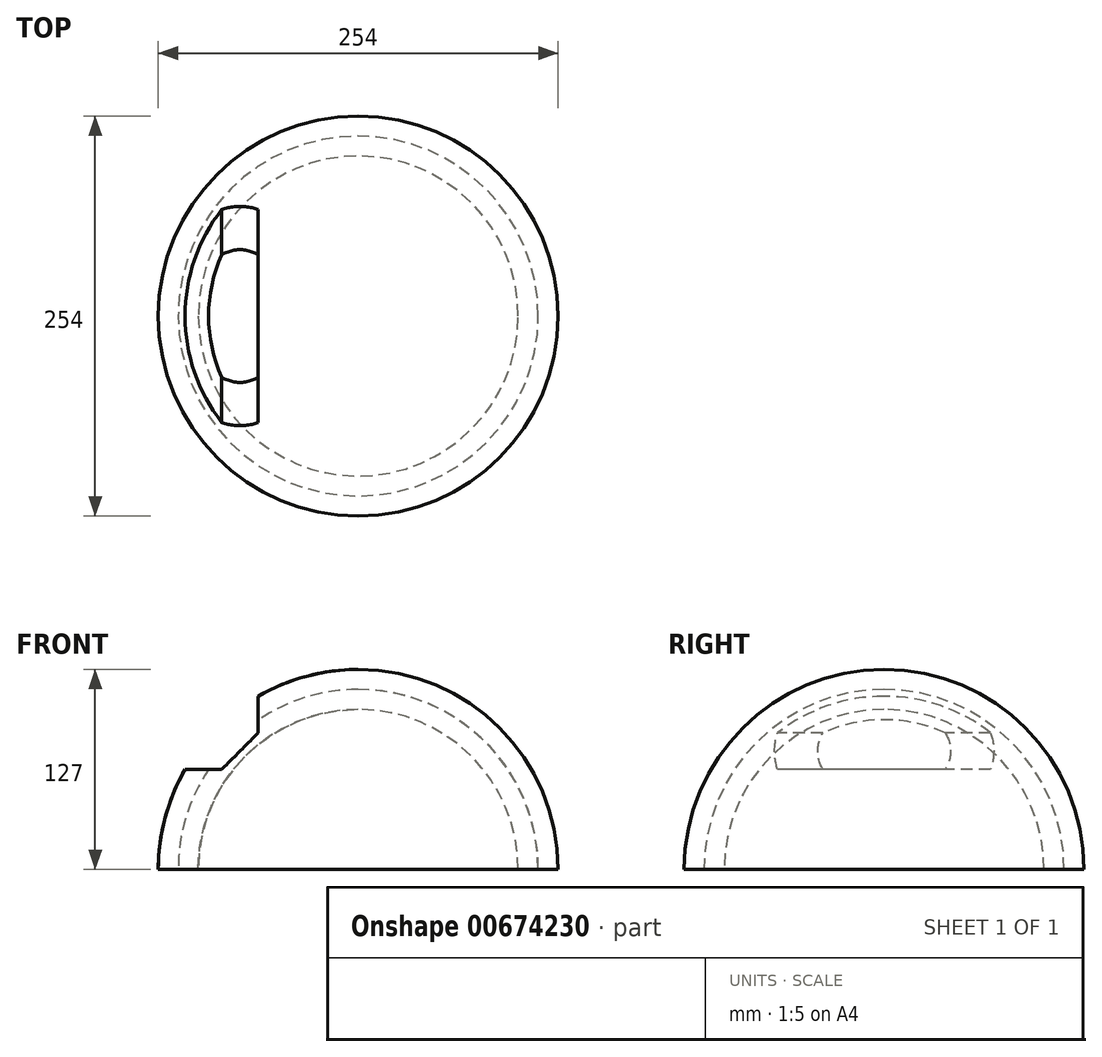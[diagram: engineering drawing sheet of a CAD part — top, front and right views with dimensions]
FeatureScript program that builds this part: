
annotation { "Feature Type Name" : "Feature", "Feature Type Description" : "" }
export const myFeature = defineFeature(function(context is Context, id is Id, definition is map)
    precondition{}
    {
        {
            var Q0;
            Q0=qCreatedBy(makeId("Front.planeOp"),FACE);
            var sketch = newSketch(context, id + "F0", { "sketchPlane" : qUnion([Q0])});
            skLineSegment(sketch, "E0.bottom", {"start": v(63.5, 63.5) * mm, "end": v(63.5, 63.5) * mm});
            skLineSegment(sketch, "E0.top", {"start": v(63.5, -63.5) * mm, "end": v(-63.5, -63.5) * mm});
            skLineSegment(sketch, "E0.left", {"start": v(63.5, 63.5) * mm, "end": v(63.5, -63.5) * mm});
            skLineSegment(sketch, "E0.right", {"start": v(-63.5, -63.5) * mm, "end": v(-63.5, -63.5) * mm});
            skPoint(sketch, "E0.middle", {"position": v(0, 0) * mm});
            skPoint(sketch, "E1.visualSharp", {"position": v(-63.5, 63.5) * mm});
            skArc(sketch, "E1.filletArc", {"start": v(63.5, 63.5) * mm, "mid": v(-26.3, 26.3) * mm, "end": v(-63.5, -63.5) * mm});
            skPoint(sketch, "E2.MirrorCS.end.orphan", {"position": v(-46.49, 0) * mm});
            skArc(sketch, "E3.0", {"start": v(63.5, 50.8) * mm, "mid": v(-17.32, 17.32) * mm, "end": v(-50.8, -63.5) * mm});
            skArc(sketch, "E4.0", {"start": v(63.5, 38.1) * mm, "mid": v(-8.34, 8.34) * mm, "end": v(-38.1, -63.5) * mm});
            skSolve(sketch);
        }
        {
            var Q0;
            {var subQ0=sQuery(id+"F0.wireOp",EDGE,"E1.filletArc");Q0=makeQuery(id+"F0.imprint","IMPRINT",FACE,{"disambiguationData":[TD([[makeQuery(id+"F0.imprint","IMPRINT",EDGE,{"derivedFrom":subQ0}),1.0]])]});}
            var Q1;
            {var subQ3=sQuery(id+"F0.wireOp",EDGE,"E4.0");Q1=makeQuery(id+"F0.imprint","IMPRINT",FACE,{"disambiguationData":[TD([[makeQuery(id+"F0.imprint","IMPRINT",EDGE,{"derivedFrom":subQ3}),1.0]])]});}
            var Q2;
            Q2=sQuery(id+"F0.wireOp",EDGE,"E0.left");
            revolve(context, id + "F1", {"entities" : qUnion([Q0, Q1]), "axis" : qUnion([Q2]), "revolveType" : RevolveType.FULL});
        }
        {
            var Q0;
            Q0=qCreatedBy(makeId("Front.planeOp"),FACE);
            var sketch = newSketch(context, id + "F2", { "sketchPlane" : qUnion([Q0])});
            skArc(sketch, "E5", {"start": v(190.5, -63.5) * mm, "mid": v(63.5, 63.5) * mm, "end": v(-63.5, -63.5) * mm});
            skLineSegment(sketch, "E6", {"start": v(-46.49, 0) * mm, "end": v(0, 46.49) * mm});
            skLineSegment(sketch, "E7", {"start": v(0, 46.49) * mm, "end": v(0, 23.24) * mm});
            skLineSegment(sketch, "E8", {"start": v(-23.24, 0) * mm, "end": v(-46.49, 0) * mm});
            skLineSegment(sketch, "E9", {"start": v(0, 23.24) * mm, "end": v(-23.24, 0) * mm});
            skPoint(sketch, "E10.orphan", {"position": v(0, 0) * mm});
            skSolve(sketch);
        }
        {
            var Q0;
            Q0 = qSketchRegion(id + "F2", true);
            extrude(context, id + "F3", {"entities" : qUnion([Q0]), "operationType" : NewBodyOperationType.REMOVE, "endBound" : BoundingType.SYMMETRIC, "oppositeDirection" : true, "depth" : 254 * mm, "offsetDistance" : 25.4 * mm});
        }
    });
